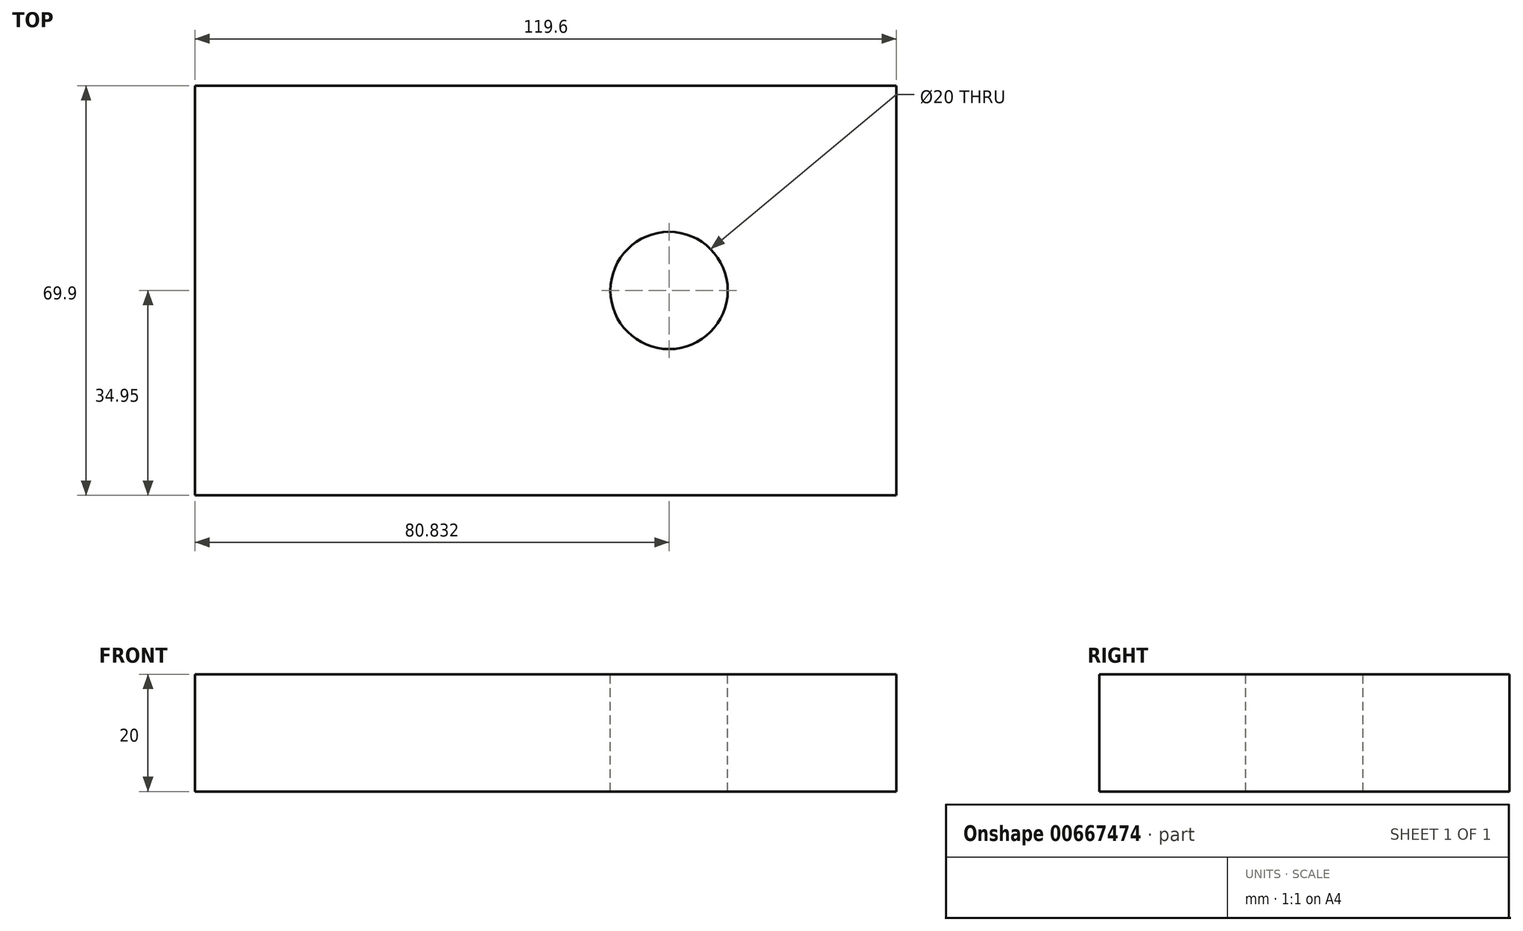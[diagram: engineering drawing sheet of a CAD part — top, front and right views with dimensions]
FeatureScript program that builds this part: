
annotation { "Feature Type Name" : "Feature", "Feature Type Description" : "" }
export const myFeature = defineFeature(function(context is Context, id is Id, definition is map)
    precondition{}
    {
        {
            var Q0;
            Q0=qCreatedBy(makeId("Top.planeOp"),FACE);
            var sketch = newSketch(context, id + "F0", { "sketchPlane" : qUnion([Q0])});
            skLineSegment(sketch, "E0.bottom", {"start": v(59.8, 34.95) * mm, "end": v(-59.8, 34.95) * mm});
            skLineSegment(sketch, "E0.top", {"start": v(59.8, -34.95) * mm, "end": v(-59.8, -34.95) * mm});
            skLineSegment(sketch, "E0.left", {"start": v(59.8, 34.95) * mm, "end": v(59.8, -34.95) * mm});
            skLineSegment(sketch, "E0.right", {"start": v(-59.8, 34.95) * mm, "end": v(-59.8, -34.95) * mm});
            skPoint(sketch, "E0.middle", {"position": v(0, 0) * mm});
            skSolve(sketch);
        }
        {
            var Q0;
            Q0=makeQuery(id+"F0.imprint","IMPRINT",FACE,{"disambiguationData":[TD([[makeQuery(id+"F0.imprint","IMPRINT",EDGE,{"derivedFrom":sQuery(id+"F0.wireOp",EDGE,"E0.bottom")}),1.0]])]});
            extrude(context, id + "F1", {"entities" : qUnion([Q0]), "depth" : 20 * mm, "offsetDistance" : 25 * mm});
        }
        {
            var Q0;
            Q0=makeQuery(id+"F1.opExtrude","CAP_FACE",FACE,{"disambiguationData":[OSD([sQuery(id+"F0.wireOp",EDGE,"E0.bottom"),sQuery(id+"F0.wireOp",EDGE,"E0.top"),sQuery(id+"F0.wireOp",EDGE,"E0.left"),sQuery(id+"F0.wireOp",EDGE,"E0.right")])],"isStart":false});
            var sketch = newSketch(context, id + "F2", { "sketchPlane" : qUnion([Q0])});
            skPoint(sketch, "E1", {"position": v(21.03, 0) * mm});
            skPoint(sketch, "E1.positionSnap0", {"position": v(59.8, 0) * mm});
            skSolve(sketch);
        }
        {
            var Q0;
            Q0=sQuery(id+"F2.wireOp",VERTEX,"E1");
            var Q1;
            Q1=makeQuery(id+"F1.opExtrude","SWEPT_BODY",BODY,{"disambiguationData":[OSD([sQuery(id+"F0.wireOp",EDGE,"E0.bottom"),sQuery(id+"F0.wireOp",EDGE,"E0.top"),sQuery(id+"F0.wireOp",EDGE,"E0.left"),sQuery(id+"F0.wireOp",EDGE,"E0.right")])]});
            hole(context, id + "F3", {"style" : HoleStyle.SIMPLE, "endStyle" : HoleEndStyle.THROUGH, "holeDiameter" : 20 * mm, "majorDiameter" : 5 * mm, "isTappedThrough" : true, "tappedDepth" : 12 * mm, "tapClearance" : 3, "startFromSketch" : true, "locations" : qUnion([Q0]), "scope" : qUnion([Q1])});
        }
    });
